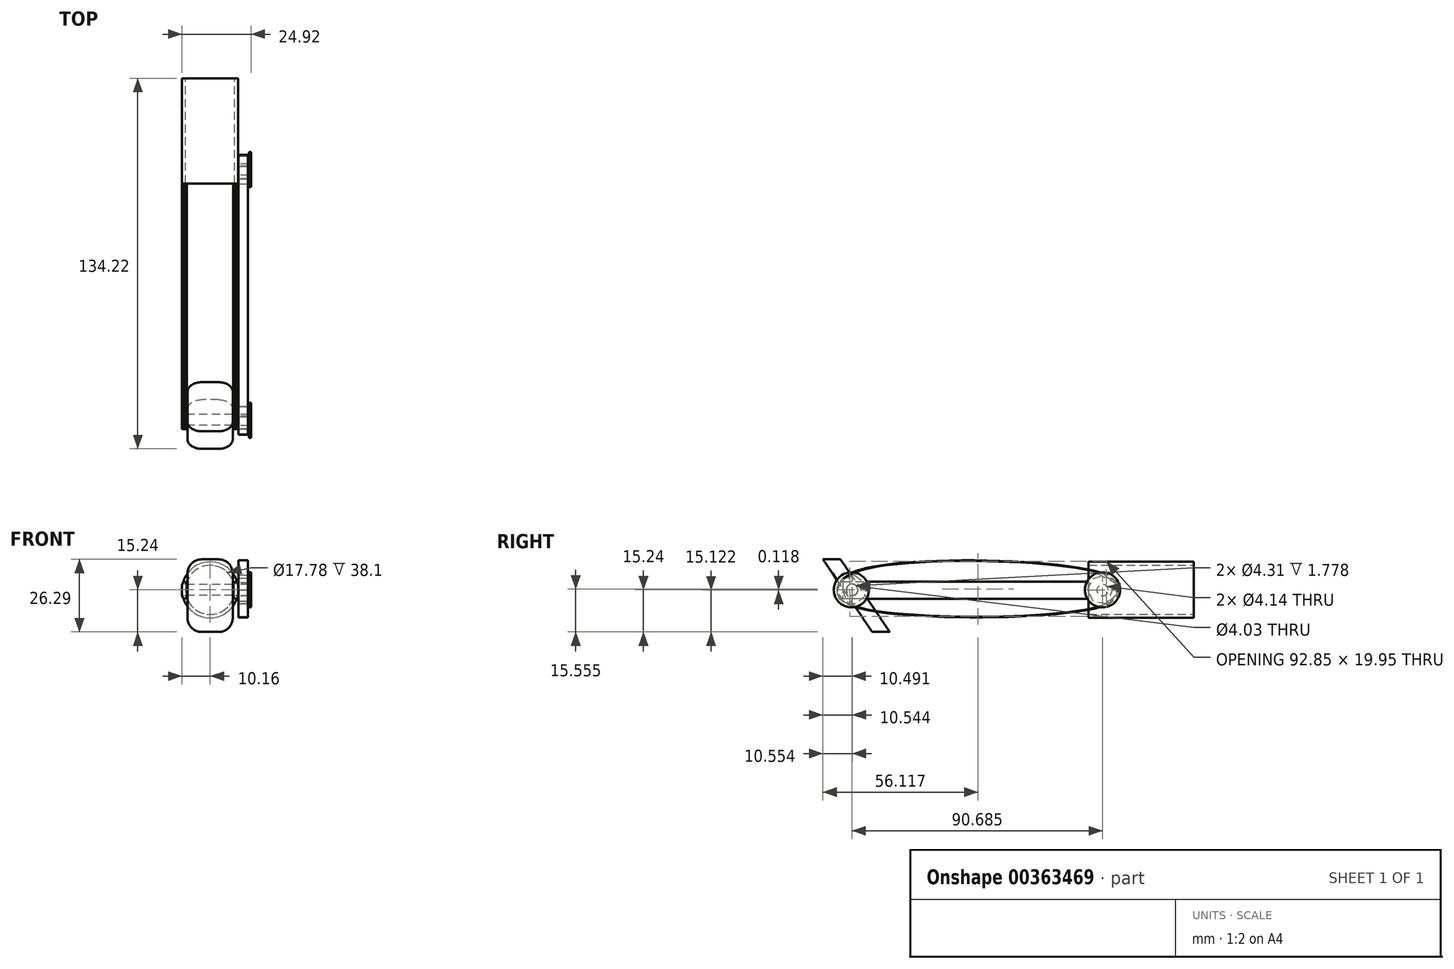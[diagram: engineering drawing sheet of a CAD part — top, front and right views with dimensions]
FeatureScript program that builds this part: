
annotation { "Feature Type Name" : "Feature", "Feature Type Description" : "" }
export const myFeature = defineFeature(function(context is Context, id is Id, definition is map)
    precondition{}
    {
        {
            var Q0;
            Q0=qCreatedBy(makeId("Right.planeOp"),FACE);
            var sketch = newSketch(context, id + "F0", { "sketchPlane" : qUnion([Q0])});
            skLineSegment(sketch, "E0.bottom", {"start": v(17.7, 10.16) * mm, "end": v(55.8, 10.16) * mm});
            skLineSegment(sketch, "E0.top", {"start": v(17.7, -10.16) * mm, "end": v(55.8, -10.16) * mm});
            skLineSegment(sketch, "E0.left", {"start": v(17.7, 10.16) * mm, "end": v(17.7, -10.16) * mm});
            skLineSegment(sketch, "E0.right", {"start": v(55.8, 10.16) * mm, "end": v(55.8, -10.16) * mm});
            skSolve(sketch);
        }
        {
            var Q0;
            Q0 = qSketchRegion(id + "F0", true);
            extrude(context, id + "F1", {"entities" : qUnion([Q0]), "endBound" : BoundingType.SYMMETRIC, "depth" : 20.32 * mm});
        }
        {
            var Q0;
            Q0=makeQuery(id+"F1.opExtrude","CAP_EDGE",EDGE,{"disambiguationData":[OSD([sQuery(id+"F0.wireOp",EDGE,"E0.bottom")])],"isStart":false});
            var Q1;
            Q1=makeQuery(id+"F1.opExtrude","CAP_EDGE",EDGE,{"disambiguationData":[OSD([sQuery(id+"F0.wireOp",EDGE,"E0.bottom")])],"isStart":true});
            var Q2;
            Q2=makeQuery(id+"F1.opExtrude","CAP_EDGE",EDGE,{"disambiguationData":[OSD([sQuery(id+"F0.wireOp",EDGE,"E0.top")])],"isStart":false});
            var Q3;
            Q3=makeQuery(id+"F1.opExtrude","CAP_EDGE",EDGE,{"disambiguationData":[OSD([sQuery(id+"F0.wireOp",EDGE,"E0.top")])],"isStart":true});
            fillet(context, id + "F2", {"entities" : qUnion([Q0, Q1, Q2, Q3]), "radius" : 10.16 * mm, "tangentPropagation" : true, "allowEdgeOverflow" : false});
        }
        {
            var Q0;
            Q0=makeQuery(id+"F1.opExtrude","SWEPT_FACE",FACE,{"disambiguationData":[OSD([sQuery(id+"F0.wireOp",EDGE,"E0.left")])]});
            var Q1;
            Q1=makeQuery(id+"F1.opExtrude","SWEPT_FACE",FACE,{"disambiguationData":[OSD([sQuery(id+"F0.wireOp",EDGE,"E0.right")])]});
            shell(context, id + "F3", {"entities" : qUnion([Q0, Q1]), "thickness" : 1.27 * mm});
        }
        {
            var Q0;
            Q0=qCreatedBy(makeId("Right.planeOp"),FACE);
            var sketch = newSketch(context, id + "F4", { "sketchPlane" : qUnion([Q0])});
            skLineSegment(sketch, "E1.bottom", {"start": v(17.68, 3.03) * mm, "end": v(-71.22, 3.03) * mm});
            skLineSegment(sketch, "E1.top", {"start": v(17.68, -3.32) * mm, "end": v(-71.22, -3.32) * mm});
            skLineSegment(sketch, "E1.left", {"start": v(17.68, 3.03) * mm, "end": v(17.68, -3.32) * mm});
            skLineSegment(sketch, "E1.right", {"start": v(-71.22, 3.03) * mm, "end": v(-71.22, -3.32) * mm});
            skCircle(sketch, "E2", {"center": v(-67.88, 0) * mm, "radius": 2.15 * mm});
            skSolve(sketch);
        }
        {
            var Q0;
            Q0=makeQuery(id+"F4.imprint","IMPRINT",FACE,{"disambiguationData":[TD([[makeQuery(id+"F4.imprint","IMPRINT",EDGE,{"derivedFrom":sQuery(id+"F4.wireOp",EDGE,"E1.bottom")}),1.0]])]});
            extrude(context, id + "F5", {"entities" : qUnion([Q0]), "depth" : 10.16 * mm, "hasSecondDirection" : true, "secondDirectionOppositeDirection" : false, "secondDirectionDepth" : 8.38 * mm});
        }
        {
            var Q0;
            Q0=makeQuery(id+"F5.opExtrude","CAP_EDGE",EDGE,{"disambiguationData":[OSD([sQuery(id+"F4.wireOp",EDGE,"E1.bottom")])],"isStart":false});
            var Q1;
            Q1=makeQuery(id+"F5.opExtrude","CAP_EDGE",EDGE,{"disambiguationData":[OSD([sQuery(id+"F4.wireOp",EDGE,"E1.top")])],"isStart":false});
            var Q2;
            Q2=makeQuery(id+"F5.opExtrude","CAP_EDGE",EDGE,{"disambiguationData":[OSD([sQuery(id+"F4.wireOp",EDGE,"E1.bottom")])],"isStart":true});
            var Q3;
            Q3=makeQuery(id+"F5.opExtrude","CAP_EDGE",EDGE,{"disambiguationData":[OSD([sQuery(id+"F4.wireOp",EDGE,"E1.top")])],"isStart":true});
            fillet(context, id + "F6", {"entities" : qUnion([Q0, Q1, Q2, Q3]), "radius" : 1.27 * mm, "tangentPropagation" : true, "allowEdgeOverflow" : false});
        }
        {
            var Q0;
            Q0=makeQuery(id+"F5.opExtrude","SWEPT_BODY",BODY,{"disambiguationData":[OSD([sQuery(id+"F4.wireOp",EDGE,"E1.bottom"),sQuery(id+"F4.wireOp",EDGE,"E1.top"),sQuery(id+"F4.wireOp",EDGE,"E1.left"),sQuery(id+"F4.wireOp",EDGE,"E1.right")])]});
            var Q1;
            Q1=qCreatedBy(makeId("Right.planeOp"),FACE);
            mirror(context, id + "F7", {"entities" : qUnion([Q0]), "mirrorPlane" : qUnion([Q1])});
        }
        {
            var Q0;
            Q0=qCreatedBy(makeId("Right.planeOp"),FACE);
            var sketch = newSketch(context, id + "F8", { "sketchPlane" : qUnion([Q0])});
            skLineSegment(sketch, "E3", {"start": v(-72.08, 11.05) * mm, "end": v(-54.27, -15.24) * mm});
            skLineSegment(sketch, "E4", {"start": v(-54.27, -15.24) * mm, "end": v(-60.62, -15.24) * mm});
            skLineSegment(sketch, "E5", {"start": v(-60.62, -15.24) * mm, "end": v(-78.43, 11.05) * mm});
            skLineSegment(sketch, "E6", {"start": v(-78.43, 11.05) * mm, "end": v(-72.08, 11.05) * mm});
            skCircle(sketch, "E7", {"center": v(-67.89, 0) * mm, "radius": 2.02 * mm});
            skSolve(sketch);
        }
        {
            var Q0;
            Q0=makeQuery(id+"F8.imprint","IMPRINT",FACE,{"disambiguationData":[TD([[makeQuery(id+"F8.imprint","IMPRINT",EDGE,{"derivedFrom":sQuery(id+"F8.wireOp",EDGE,"E3")}),-1.0]])]});
            extrude(context, id + "F9", {"entities" : qUnion([Q0]), "endBound" : BoundingType.SYMMETRIC, "depth" : 16.38 * mm});
        }
        {
            var Q0;
            Q0=makeQuery(id+"F9.opExtrude","CAP_EDGE",EDGE,{"disambiguationData":[OSD([sQuery(id+"F8.wireOp",EDGE,"E4")])],"isStart":false});
            var Q1;
            Q1=makeQuery(id+"F9.opExtrude","CAP_EDGE",EDGE,{"disambiguationData":[OSD([sQuery(id+"F8.wireOp",EDGE,"E4")])],"isStart":true});
            var Q2;
            Q2=makeQuery(id+"F9.opExtrude","CAP_EDGE",EDGE,{"disambiguationData":[OSD([sQuery(id+"F8.wireOp",EDGE,"E6")])],"isStart":true});
            var Q3;
            Q3=makeQuery(id+"F9.opExtrude","CAP_EDGE",EDGE,{"disambiguationData":[OSD([sQuery(id+"F8.wireOp",EDGE,"E6")])],"isStart":false});
            fillet(context, id + "F10", {"entities" : qUnion([Q0, Q1, Q2, Q3]), "radius" : 5.08 * mm, "tangentPropagation" : true, "allowEdgeOverflow" : false});
        }
        {
            var Q0;
            Q0=qCreatedBy(makeId("Right.planeOp"),FACE);
            var sketch = newSketch(context, id + "F11", { "sketchPlane" : qUnion([Q0])});
            skCircle(sketch, "E8.cCircle", {"center": v(-67.94, 0) * mm, "radius": 5.32 * mm, "construction": true});
            skLineSegment(sketch, "E8.0", {"start": v(-63.22, 2.46) * mm, "end": v(-63.07, -2.16) * mm});
            skLineSegment(sketch, "E8.1", {"start": v(-63.07, -2.16) * mm, "end": v(-66.6, -5.15) * mm});
            skLineSegment(sketch, "E8.2", {"start": v(-66.6, -5.15) * mm, "end": v(-71.13, -4.26) * mm});
            skLineSegment(sketch, "E8.3", {"start": v(-71.13, -4.26) * mm, "end": v(-73.26, -0.16) * mm});
            skLineSegment(sketch, "E8.4", {"start": v(-73.26, -0.16) * mm, "end": v(-71.38, 4.06) * mm});
            skLineSegment(sketch, "E8.5", {"start": v(-71.38, 4.06) * mm, "end": v(-66.91, 5.22) * mm});
            skLineSegment(sketch, "E8.6", {"start": v(-66.91, 5.22) * mm, "end": v(-63.22, 2.46) * mm});
            skCircle(sketch, "E9.cCircle", {"center": v(22.65, 0.1) * mm, "radius": 5.32 * mm, "construction": true});
            skLineSegment(sketch, "E9.0", {"start": v(27.38, 2.55) * mm, "end": v(27.52, -2.07) * mm});
            skLineSegment(sketch, "E9.1", {"start": v(27.52, -2.07) * mm, "end": v(24, -5.06) * mm});
            skLineSegment(sketch, "E9.2", {"start": v(24, -5.06) * mm, "end": v(19.46, -4.17) * mm});
            skLineSegment(sketch, "E9.3", {"start": v(19.46, -4.17) * mm, "end": v(17.33, -0.07) * mm});
            skLineSegment(sketch, "E9.4", {"start": v(17.33, -0.07) * mm, "end": v(19.2, 4.15) * mm});
            skLineSegment(sketch, "E9.5", {"start": v(19.2, 4.15) * mm, "end": v(23.68, 5.32) * mm});
            skLineSegment(sketch, "E9.6", {"start": v(23.68, 5.32) * mm, "end": v(27.38, 2.55) * mm});
            skCircle(sketch, "E10", {"center": v(-67.94, 0) * mm, "radius": 2.07 * mm});
            skCircle(sketch, "E11", {"center": v(22.75, -0.12) * mm, "radius": 2.07 * mm});
            skSolve(sketch);
        }
        {
            var Q0;
            Q0=makeQuery(id+"F11.imprint","IMPRINT",FACE,{"disambiguationData":[TD([[makeQuery(id+"F11.imprint","IMPRINT",EDGE,{"derivedFrom":sQuery(id+"F11.wireOp",EDGE,"E8.0")}),-1.0]])]});
            var Q1;
            Q1=makeQuery(id+"F11.imprint","IMPRINT",FACE,{"disambiguationData":[TD([[makeQuery(id+"F11.imprint","IMPRINT",EDGE,{"derivedFrom":sQuery(id+"F11.wireOp",EDGE,"E9.0")}),-1.0]])]});
            extrude(context, id + "F12", {"entities" : qUnion([Q0, Q1]), "depth" : 13.97 * mm, "hasSecondDirection" : true, "secondDirectionOppositeDirection" : false, "secondDirectionDepth" : 10.29 * mm});
        }
        {
            var Q0;
            Q0=qCreatedBy(makeId("Right.planeOp"),FACE);
            var sketch = newSketch(context, id + "F13", { "sketchPlane" : qUnion([Q0])});
            skCircle(sketch, "E12", {"center": v(-68.14, 0) * mm, "radius": 6.35 * mm});
            skCircle(sketch, "E13", {"center": v(22.73, 0) * mm, "radius": 6.35 * mm});
            skSolve(sketch);
        }
        {
            var Q0;
            Q0=makeQuery(id+"F13.imprint","IMPRINT",FACE,{"disambiguationData":[TD([[makeQuery(id+"F13.imprint","IMPRINT",EDGE,{"derivedFrom":sQuery(id+"F13.wireOp",EDGE,"E13")}),1.0]])]});
            var Q1;
            Q1=makeQuery(id+"F13.imprint","IMPRINT",FACE,{"disambiguationData":[TD([[makeQuery(id+"F13.imprint","IMPRINT",EDGE,{"derivedFrom":sQuery(id+"F13.wireOp",EDGE,"E12")}),1.0]])]});
            extrude(context, id + "F14", {"entities" : qUnion([Q0, Q1]), "depth" : 14.76 * mm, "hasSecondDirection" : true, "secondDirectionOppositeDirection" : false, "secondDirectionDepth" : 14.05 * mm});
        }
        {
            var Q0;
            Q0=qCreatedBy(makeId("Right.planeOp"),FACE);
            var sketch = newSketch(context, id + "F15", { "sketchPlane" : qUnion([Q0])});
            skFitSpline(sketch, "E14", {"points": [v(-65.33, 7.22) * mm, v(24.21, 5.5) * mm, v(28.06, 0) * mm, v(24.21, -5.42) * mm, v(-67.14, -6.18) * mm, v(-73.3, 0) * mm, v(-65.33, 7.22) * mm]});
            skSolve(sketch);
        }
        {
            var Q0;
            Q0=makeQuery(id+"F15.imprint","IMPRINT",FACE,{"disambiguationData":[TD([[makeQuery(id+"F15.imprint","IMPRINT",EDGE,{"derivedFrom":sQuery(id+"F15.wireOp",EDGE,"E14")}),-1.0]])]});
            extrude(context, id + "F16", {"entities" : qUnion([Q0]), "depth" : 13.72 * mm, "hasSecondDirection" : true, "secondDirectionOppositeDirection" : false, "secondDirectionDepth" : 10.3 * mm});
        }
        {
            var Q0;
            Q0=makeQuery(id+"F16.opExtrude","CAP_FACE",FACE,{"disambiguationData":[OSD([sQuery(id+"F15.wireOp",EDGE,"E14")])],"isStart":false});
            var Q1;
            Q1=makeQuery(id+"F16.opExtrude","CAP_FACE",FACE,{"disambiguationData":[OSD([sQuery(id+"F15.wireOp",EDGE,"E14")])],"isStart":true});
            shell(context, id + "F17", {"entities" : qUnion([Q0, Q1]), "thickness" : 0.25 * mm});
        }
    });
